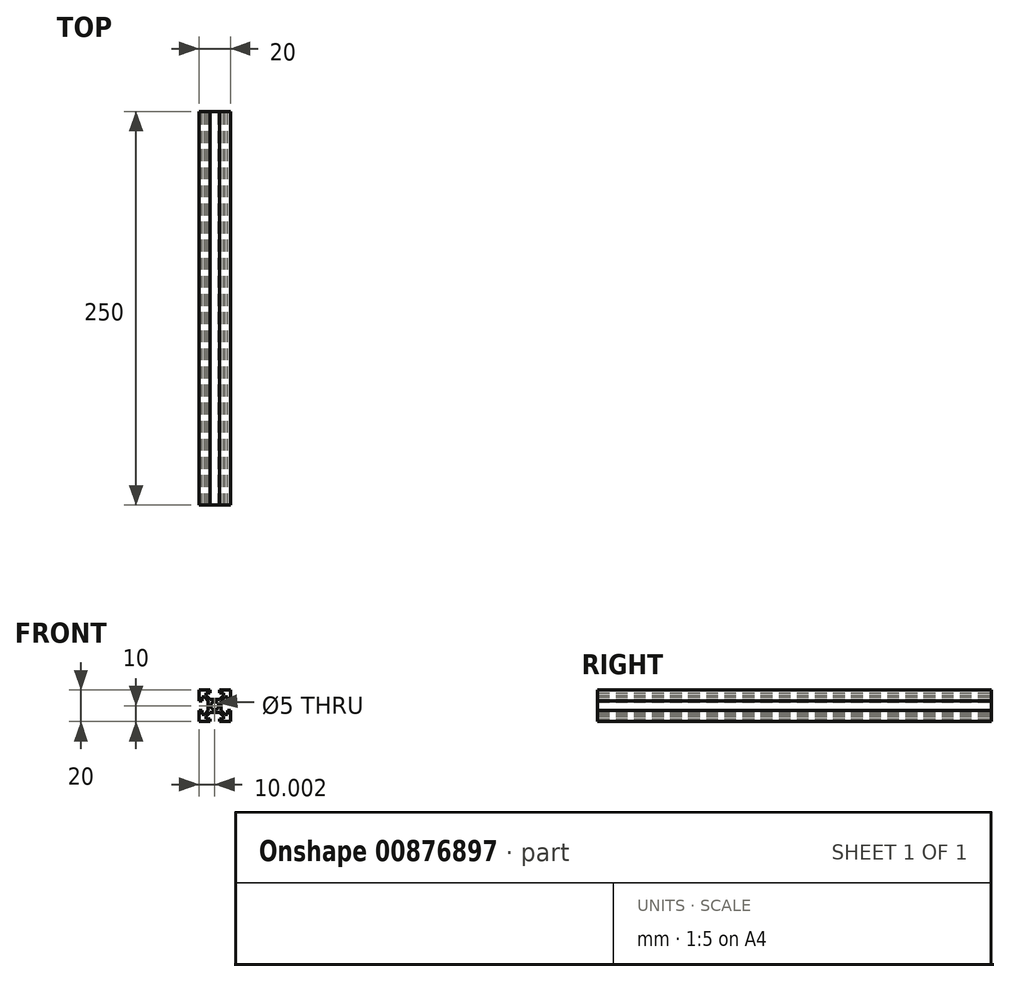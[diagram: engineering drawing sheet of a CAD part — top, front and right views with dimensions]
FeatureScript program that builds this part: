
annotation { "Feature Type Name" : "Feature", "Feature Type Description" : "" }
export const myFeature = defineFeature(function(context is Context, id is Id, definition is map)
    precondition{}
    {
        {
            var Q0;
            Q0=qCreatedBy(makeId("Front.planeOp"),FACE);
            var sketch = newSketch(context, id + "F0", { "sketchPlane" : qUnion([Q0])});
            skLineSegment(sketch, "E0.bottom", {"start": v(-65.2, 69.4) * mm, "end": v(-45.2, 69.4) * mm});
            skLineSegment(sketch, "E0.top", {"start": v(-65.2, 49.4) * mm, "end": v(-45.2, 49.4) * mm});
            skLineSegment(sketch, "E0.left", {"start": v(-65.2, 69.4) * mm, "end": v(-65.2, 49.4) * mm});
            skLineSegment(sketch, "E0.right", {"start": v(-45.2, 69.4) * mm, "end": v(-45.2, 49.4) * mm});
            skPoint(sketch, "E0.middle", {"position": v(-55.2, 59.4) * mm});
            skLineSegment(sketch, "E1", {"start": v(-47, 62.5) * mm, "end": v(-45.2, 62.5) * mm});
            skLineSegment(sketch, "E2.MirrorCS", {"start": v(-47, 56.3) * mm, "end": v(-45.2, 56.3) * mm});
            skLineSegment(sketch, "E3", {"start": v(-47, 62.5) * mm, "end": v(-47, 64.9) * mm});
            skLineSegment(sketch, "E4.MirrorCS", {"start": v(-47, 56.3) * mm, "end": v(-47, 53.9) * mm});
            skLineSegment(sketch, "E5", {"start": v(-47, 64.9) * mm, "end": v(-48.6, 64.9) * mm});
            skLineSegment(sketch, "E6.MirrorCS", {"start": v(-47, 53.9) * mm, "end": v(-48.6, 53.9) * mm});
            skCircle(sketch, "E7", {"center": v(-55.2, 59.4) * mm, "radius": 2.5 * mm});
            skLineSegment(sketch, "E8", {"start": v(-51.1, 62.4) * mm, "end": v(-51.1, 56.4) * mm});
            skLineSegment(sketch, "E9", {"start": v(-51.1, 62.4) * mm, "end": v(-48.6, 64.9) * mm});
            skLineSegment(sketch, "E10.MirrorCS", {"start": v(-51.1, 56.4) * mm, "end": v(-48.6, 53.9) * mm});
            skLineSegment(sketch, "E11.MirrorCS", {"start": v(-63.4, 62.5) * mm, "end": v(-65.2, 62.5) * mm});
            skLineSegment(sketch, "E12.MirrorCS", {"start": v(-63.4, 62.5) * mm, "end": v(-63.4, 64.9) * mm});
            skLineSegment(sketch, "E13.MirrorCS", {"start": v(-63.4, 64.9) * mm, "end": v(-61.8, 64.9) * mm});
            skLineSegment(sketch, "E14.MirrorCS", {"start": v(-59.3, 62.4) * mm, "end": v(-61.8, 64.9) * mm});
            skLineSegment(sketch, "E15.MirrorCS", {"start": v(-59.3, 62.4) * mm, "end": v(-59.3, 56.4) * mm});
            skLineSegment(sketch, "E16.MirrorCS", {"start": v(-59.3, 56.4) * mm, "end": v(-61.8, 53.9) * mm});
            skLineSegment(sketch, "E17.MirrorCS", {"start": v(-63.4, 53.9) * mm, "end": v(-61.8, 53.9) * mm});
            skLineSegment(sketch, "E18.MirrorCS", {"start": v(-63.4, 56.3) * mm, "end": v(-63.4, 53.9) * mm});
            skLineSegment(sketch, "E19.MirrorCS", {"start": v(-63.4, 56.3) * mm, "end": v(-65.2, 56.3) * mm});
            skLineSegment(sketch, "E20", {"start": v(-58.3, 69.4) * mm, "end": v(-58.3, 67.6) * mm});
            skLineSegment(sketch, "E21", {"start": v(-58.3, 67.6) * mm, "end": v(-60.7, 67.6) * mm});
            skLineSegment(sketch, "E22", {"start": v(-60.7, 67.6) * mm, "end": v(-60.7, 66) * mm});
            skLineSegment(sketch, "E23", {"start": v(-58.2, 63.5) * mm, "end": v(-55.2, 63.5) * mm});
            skLineSegment(sketch, "E24.MirrorCS", {"start": v(-52.1, 69.4) * mm, "end": v(-52.1, 67.6) * mm});
            skLineSegment(sketch, "E25.MirrorCS", {"start": v(-52.1, 67.6) * mm, "end": v(-49.7, 67.6) * mm});
            skLineSegment(sketch, "E26.MirrorCS", {"start": v(-49.7, 67.6) * mm, "end": v(-49.7, 66) * mm});
            skLineSegment(sketch, "E27.MirrorCS", {"start": v(-52.2, 63.5) * mm, "end": v(-55.2, 63.5) * mm});
            skLineSegment(sketch, "E28", {"start": v(-49.7, 66) * mm, "end": v(-52.2, 63.5) * mm});
            skLineSegment(sketch, "E29", {"start": v(-60.7, 66) * mm, "end": v(-58.2, 63.5) * mm});
            skLineSegment(sketch, "E30.MirrorCS", {"start": v(-58.3, 49.4) * mm, "end": v(-58.3, 51.2) * mm});
            skLineSegment(sketch, "E31.MirrorCS", {"start": v(-58.3, 51.2) * mm, "end": v(-60.7, 51.2) * mm});
            skLineSegment(sketch, "E32.MirrorCS", {"start": v(-60.7, 51.2) * mm, "end": v(-60.7, 52.8) * mm});
            skLineSegment(sketch, "E33.MirrorCS", {"start": v(-60.7, 52.8) * mm, "end": v(-58.2, 55.3) * mm});
            skLineSegment(sketch, "E34.MirrorCS", {"start": v(-52.1, 49.4) * mm, "end": v(-52.1, 51.2) * mm});
            skLineSegment(sketch, "E35.MirrorCS", {"start": v(-52.1, 51.2) * mm, "end": v(-49.7, 51.2) * mm});
            skLineSegment(sketch, "E36.MirrorCS", {"start": v(-49.7, 51.2) * mm, "end": v(-49.7, 52.8) * mm});
            skLineSegment(sketch, "E37.MirrorCS", {"start": v(-49.7, 52.8) * mm, "end": v(-52.2, 55.3) * mm});
            skLineSegment(sketch, "E38.MirrorCS", {"start": v(-52.2, 55.3) * mm, "end": v(-55.2, 55.3) * mm});
            skLineSegment(sketch, "E39.MirrorCS", {"start": v(-58.2, 55.3) * mm, "end": v(-55.2, 55.3) * mm});
            skSolve(sketch);
        }
        {
            var Q0;
            {var subQ5=sQuery(id+"F0.wireOp",EDGE,"E1");Q0=makeQuery(id+"F0.imprint","IMPRINT",FACE,{"disambiguationData":[TD([[makeQuery(id+"F0.imprint","IMPRINT",EDGE,{"derivedFrom":subQ5}),1.0]])]});}
            extrude(context, id + "F1", {"entities" : qUnion([Q0]), "depth" : 250 * mm, "offsetDistance" : 25 * mm});
        }
    });
